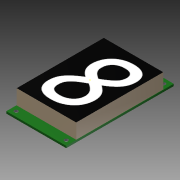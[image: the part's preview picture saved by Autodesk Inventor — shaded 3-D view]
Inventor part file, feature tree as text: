
AUTODESK INVENTOR PART (.ipt)
format: ipt  version: 2015 (Build 190159000, 159)  size: 108,544 bytes
history: native  units: mm
features: sketch x4, extrude x3, other x1
ambient origin geometry x8: Origin, YZ Plane, XZ Plane, XY Plane, X Axis, Y Axis, Z Axis, Center Point
bodies: Body1 (feature_tree)
feature tree (8):
  other  "ソリッド1"
  extrude  "押し出し1"  Depth=48.0mm
  extrude  "押し出し2"  Depth=86.0mm
  extrude  "押し出し3"  Depth=1.6mm TaperAngle=0.0deg
  sketch  "スケッチ4"
  sketch  "スケッチ1"
  sketch  "スケッチ2"
  sketch  "スケッチ3"
